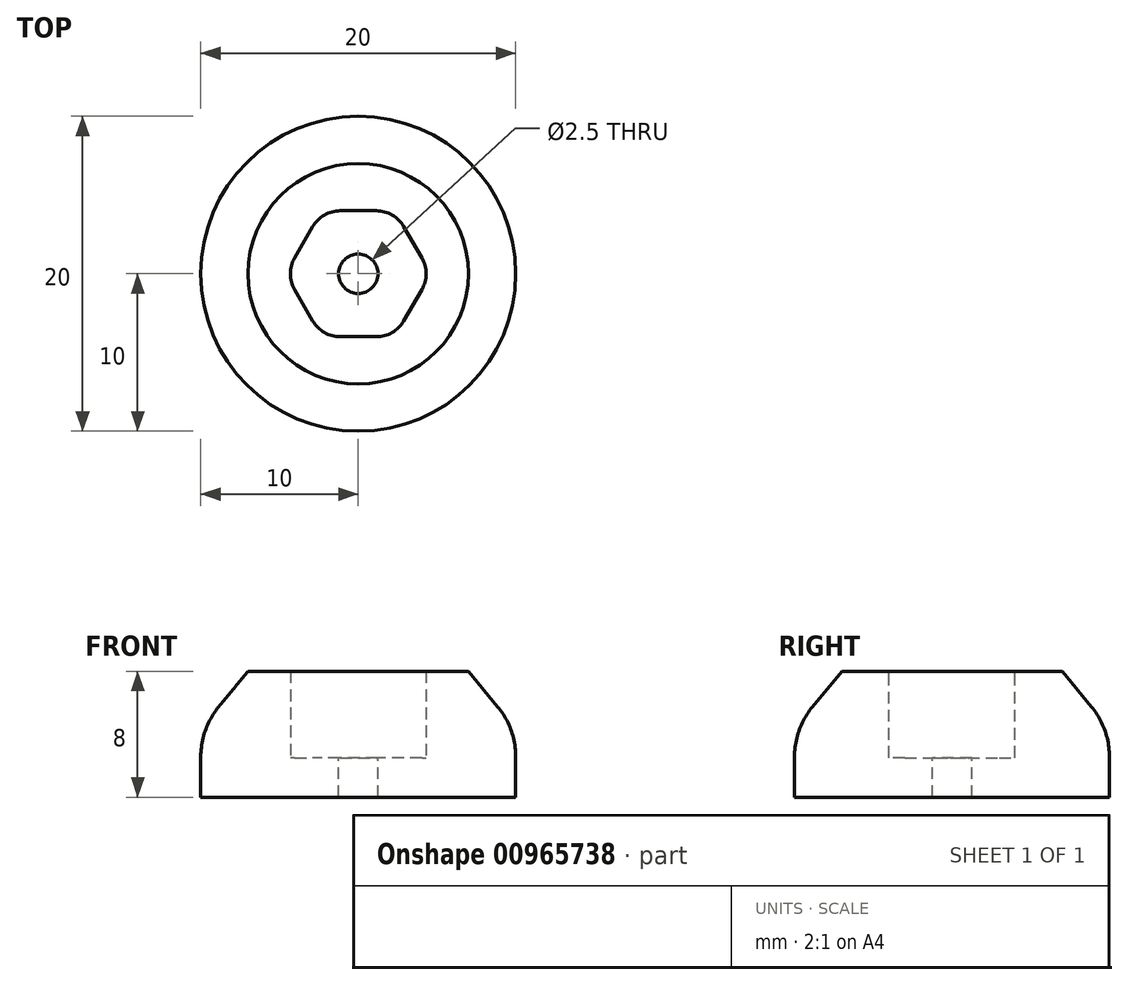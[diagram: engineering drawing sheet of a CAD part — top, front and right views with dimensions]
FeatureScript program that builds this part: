
annotation { "Feature Type Name" : "Feature", "Feature Type Description" : "" }
export const myFeature = defineFeature(function(context is Context, id is Id, definition is map)
    precondition{}
    {
        {
            var Q0;
            Q0=qCreatedBy(makeId("Front.planeOp"),FACE);
            var sketch = newSketch(context, id + "F0", { "sketchPlane" : qUnion([Q0])});
            skLineSegment(sketch, "E0", {"start": v(0, 0) * mm, "end": v(10, 0) * mm});
            skLineSegment(sketch, "E1", {"start": v(10, 0) * mm, "end": v(10, 2.57) * mm});
            skLineSegment(sketch, "E2", {"start": v(8.86, 5.75) * mm, "end": v(7, 8) * mm});
            skLineSegment(sketch, "E3", {"start": v(7, 8) * mm, "end": v(0, 8) * mm});
            skLineSegment(sketch, "E4", {"start": v(0, 8) * mm, "end": v(0, 0) * mm});
            skPoint(sketch, "E5.visualSharp", {"position": v(10, 4.36) * mm});
            skArc(sketch, "E5.filletArc", {"start": v(10, 2.57) * mm, "mid": v(9.7, 4.26) * mm, "end": v(8.86, 5.75) * mm});
            skLineSegment(sketch, "E6", {"start": v(0, -31.06) * mm, "end": v(0, 44.63) * mm, "construction": true});
            skSolve(sketch);
        }
        {
            var Q0;
            Q0 = qSketchRegion(id + "F0", true);
            var Q1;
            Q1=sQuery(id+"F0.wireOp",EDGE,"E6");
            revolve(context, id + "F1", {"surfaceOperationType" : NewSurfaceOperationType.NEW, "entities" : qUnion([Q0]), "axis" : qUnion([Q1]), "revolveType" : RevolveType.FULL});
        }
        {
            var Q0;
            Q0=makeQuery(id+"F1.opRevolve","SWEPT_FACE",FACE,{"disambiguationData":[OSD([sQuery(id+"F0.wireOp",EDGE,"E3")])]});
            var sketch = newSketch(context, id + "F2", { "sketchPlane" : qUnion([Q0])});
            skCircle(sketch, "E7.cCircle", {"center": v(0, 0) * mm, "radius": 4 * mm, "construction": true});
            skLineSegment(sketch, "E7.0", {"start": v(-2.3, 4) * mm, "end": v(2.3, 4) * mm});
            skLineSegment(sketch, "E7.1", {"start": v(2.3, 4) * mm, "end": v(4.62, 0) * mm});
            skLineSegment(sketch, "E7.2", {"start": v(4.62, 0) * mm, "end": v(2.3, -4) * mm});
            skLineSegment(sketch, "E7.3", {"start": v(2.3, -4) * mm, "end": v(-2.3, -4) * mm});
            skLineSegment(sketch, "E7.4", {"start": v(-2.3, -4) * mm, "end": v(-4.62, 0) * mm});
            skLineSegment(sketch, "E7.5", {"start": v(-4.62, 0) * mm, "end": v(-2.3, 4) * mm});
            skPoint(sketch, "E7.0.midPoint", {"position": v(0, 4) * mm});
            skSolve(sketch);
        }
        {
            var Q0;
            Q0 = qSketchRegion(id + "F2", true);
            extrude(context, id + "F3", {"entities" : qUnion([Q0]), "operationType" : NewBodyOperationType.REMOVE, "oppositeDirection" : true, "depth" : 5.5 * mm, "offsetDistance" : 25 * mm});
        }
        {
            var Q0;
            Q0=makeQuery(id+"F3.boolean.opBoolean","COPY",FACE,{"derivedFrom":makeQuery(id+"F3.opExtrude","CAP_FACE",FACE,{"disambiguationData":[OSD([sQuery(id+"F2.wireOp",EDGE,"E7.0"),sQuery(id+"F2.wireOp",EDGE,"E7.1"),sQuery(id+"F2.wireOp",EDGE,"E7.2"),sQuery(id+"F2.wireOp",EDGE,"E7.3"),sQuery(id+"F2.wireOp",EDGE,"E7.4"),sQuery(id+"F2.wireOp",EDGE,"E7.5")])],"isStart":false})});
            var sketch = newSketch(context, id + "F4", { "sketchPlane" : qUnion([Q0])});
            skCircle(sketch, "E8", {"center": v(0, 0) * mm, "radius": 1.25 * mm});
            skSolve(sketch);
        }
        {
            var Q0;
            Q0 = qSketchRegion(id + "F4", true);
            extrude(context, id + "F5", {"entities" : qUnion([Q0]), "operationType" : NewBodyOperationType.REMOVE, "oppositeDirection" : true, "depth" : 3 * mm, "offsetDistance" : 25 * mm});
        }
        {
            var Q0;
            Q0=makeQuery(id+"F3.boolean.opBoolean","COPY",EDGE,{"derivedFrom":makeQuery(id+"F3.opExtrude","SWEPT_EDGE",EDGE,{"disambiguationData":[OSD([sQuery(id+"F2.wireOp",EDGE,"E7.0"),sQuery(id+"F2.wireOp",EDGE,"E7.5")])]})});
            var Q1;
            Q1=makeQuery(id+"F3.boolean.opBoolean","COPY",EDGE,{"derivedFrom":makeQuery(id+"F3.opExtrude","SWEPT_EDGE",EDGE,{"disambiguationData":[OSD([sQuery(id+"F2.wireOp",EDGE,"E7.0"),sQuery(id+"F2.wireOp",EDGE,"E7.1")])]})});
            var Q2;
            Q2=makeQuery(id+"F3.boolean.opBoolean","COPY",EDGE,{"derivedFrom":makeQuery(id+"F3.opExtrude","SWEPT_EDGE",EDGE,{"disambiguationData":[OSD([sQuery(id+"F2.wireOp",EDGE,"E7.3"),sQuery(id+"F2.wireOp",EDGE,"E7.4")])]})});
            var Q3;
            Q3=makeQuery(id+"F3.boolean.opBoolean","COPY",EDGE,{"derivedFrom":makeQuery(id+"F3.opExtrude","SWEPT_EDGE",EDGE,{"disambiguationData":[OSD([sQuery(id+"F2.wireOp",EDGE,"E7.2"),sQuery(id+"F2.wireOp",EDGE,"E7.3")])]})});
            var Q4;
            Q4=makeQuery(id+"F3.boolean.opBoolean","COPY",EDGE,{"derivedFrom":makeQuery(id+"F3.opExtrude","SWEPT_EDGE",EDGE,{"disambiguationData":[OSD([sQuery(id+"F2.wireOp",EDGE,"E7.4"),sQuery(id+"F2.wireOp",EDGE,"E7.5")])]})});
            var Q5;
            Q5=makeQuery(id+"F3.boolean.opBoolean","COPY",EDGE,{"derivedFrom":makeQuery(id+"F3.opExtrude","SWEPT_EDGE",EDGE,{"disambiguationData":[OSD([sQuery(id+"F2.wireOp",EDGE,"E7.1"),sQuery(id+"F2.wireOp",EDGE,"E7.2")])]})});
            fillet(context, id + "F6", {"entities" : qUnion([Q0, Q1, Q2, Q3, Q4, Q5]), "radius" : 2 * mm, "tangentPropagation" : true, "allowEdgeOverflow" : false});
        }
    });
